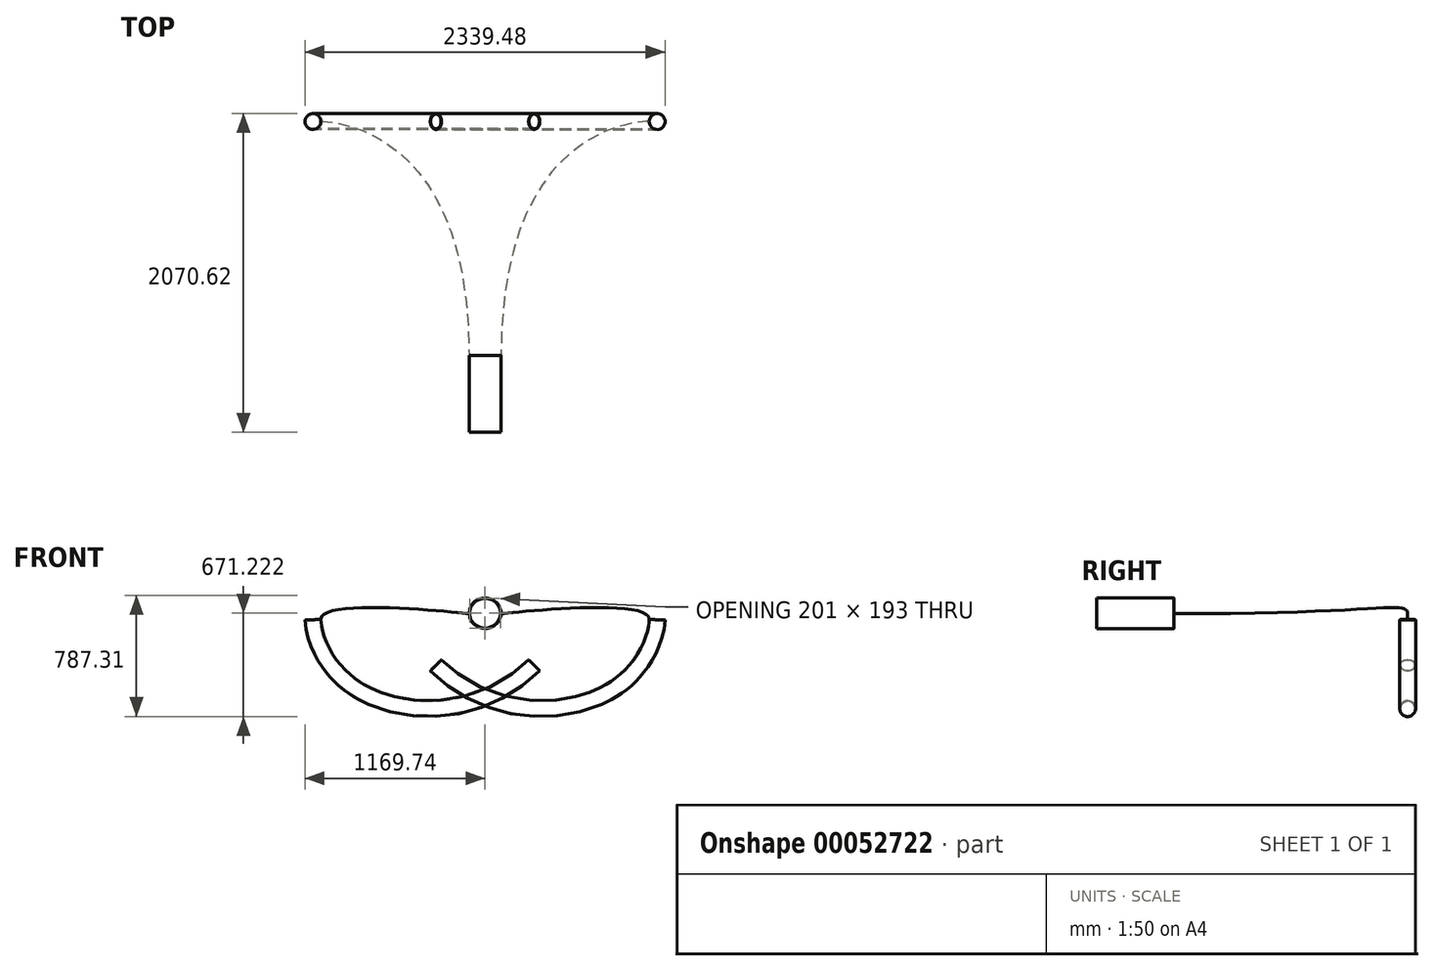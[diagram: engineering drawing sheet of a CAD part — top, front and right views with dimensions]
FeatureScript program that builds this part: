
annotation { "Feature Type Name" : "Feature", "Feature Type Description" : "" }
export const myFeature = defineFeature(function(context is Context, id is Id, definition is map)
    precondition{}
    {
        {
            var Q0;
            Q0=qCreatedBy(makeId("Front.planeOp"),FACE);
            var sketch = newSketch(context, id + "F0", { "sketchPlane" : qUnion([Q0])});
            skLineSegment(sketch, "E0", {"start": v(-822.07, 0) * mm, "end": v(894.41, 0) * mm, "construction": true});
            skLineSegment(sketch, "E1", {"start": v(0, 0) * mm, "end": v(0, 896.06) * mm, "construction": true});
            skLineSegment(sketch, "E2", {"start": v(0, 0) * mm, "end": v(-727.65, 727.65) * mm, "construction": true});
            skLineSegment(sketch, "E3", {"start": v(-854.93, 727.65) * mm, "end": v(-992.18, 590.4) * mm, "construction": true});
            skPoint(sketch, "E4.visualSharp", {"position": v(-791.3, 791.3) * mm});
            skArc(sketch, "E4.filletArc", {"start": v(-727.65, 727.65) * mm, "mid": v(-791.3, 754.01) * mm, "end": v(-854.93, 727.65) * mm, "construction": true});
            skFitSpline(sketch, "E5", {"points": [v(-992.18, 590.4) * mm, v(-770.63, 598.25) * mm, v(-520.2, 137.68) * mm], "startDerivative": vector(522.47, 522.47) * mm, "endDerivative": vector(47.32, -1250.13) * mm});
            skPoint(sketch, "E6", {"position": v(-848.51, 631.85) * mm});
            skFitSpline(sketch, "E7", {"points": [v(1112.9, 903.67) * mm, v(1334.45, 911.52) * mm, v(1584.9, 450.95) * mm], "startDerivative": vector(522.47, 522.47) * mm, "endDerivative": vector(47.32, -1250.13) * mm});
            skPoint(sketch, "E8", {"position": v(-555, 332.37) * mm});
            skSolve(sketch);
        }
        {
            var Q0;
            Q0=sQuery(id+"F0.wireOp",EDGE,"E2");
            var Q1;
            Q1=qCreatedBy(makeId("Top.planeOp"),FACE);
            cPlane(context, id + "F1", {"entities" : qUnion([Q0, Q1]), "cplaneType" : CPlaneType.LINE_ANGLE, "offset" : 150 * mm, "angle" : 0 * degree, "width" : 150 * mm, "height" : 150 * mm});
        }
        {
            var Q0;
            Q0=qCreatedBy(id+"F1.planeOp",FACE);
            cPlane(context, id + "F2", {"entities" : qUnion([Q0]), "cplaneType" : CPlaneType.OFFSET, "offset" : 284.1 * mm, "width" : 150 * mm, "height" : 150 * mm});
        }
        {
            var Q0;
            Q0=qCreatedBy(id+"F2.planeOp",FACE);
            var sketch = newSketch(context, id + "F3", { "sketchPlane" : qUnion([Q0])});
            skCircle(sketch, "E9", {"center": v(-1119.06, 0) * mm, "radius": 51.5 * mm});
            skSolve(sketch);
        }
        {
            var Q0;
            Q0=makeQuery(id+"F3.imprint","IMPRINT",FACE,{"disambiguationData":[TD([[makeQuery(id+"F3.imprint","IMPRINT",EDGE,{"derivedFrom":sQuery(id+"F3.wireOp",EDGE,"E9")}),1.0]])]});
            var Q1;
            Q1=sQuery(id+"F0.wireOp",EDGE,"E5");
            sweep(context, id + "F4", {"profiles" : qUnion([Q0]), "path" : qUnion([Q1])});
        }
        {
            var Q0;
            Q0=qCreatedBy(makeId("Right.planeOp"),FACE);
            cPlane(context, id + "F5", {"entities" : qUnion([Q0]), "cplaneType" : CPlaneType.OFFSET, "offset" : 520.2 * mm, "oppositeDirection" : true, "width" : 150 * mm, "height" : 150 * mm});
        }
        {
            var Q0;
            Q0=makeQuery(id+"F4.opSweep","SWEPT_BODY",BODY,{"disambiguationData":[OSD([sQuery(id+"F0.wireOp",EDGE,"E5"),sQuery(id+"F3.wireOp",EDGE,"E9")])]});
            var Q1;
            Q1=qCreatedBy(id+"F5.planeOp",FACE);
            mirror(context, id + "F6", {"entities" : qUnion([Q0]), "mirrorPlane" : qUnion([Q1])});
        }
        {
            var Q0;
            Q0=qCreatedBy(makeId("Front.planeOp"),FACE);
            cPlane(context, id + "F7", {"entities" : qUnion([Q0]), "cplaneType" : CPlaneType.OFFSET, "offset" : 400 * mm, "width" : 150 * mm, "height" : 150 * mm});
        }
        {
            var Q0;
            Q0=qCreatedBy(id+"F7.planeOp",FACE);
            var sketch = newSketch(context, id + "F8", { "sketchPlane" : qUnion([Q0])});
            skEllipse(sketch, "E10", {"center": v(-520.2, 137.68) * mm, "majorRadius": 104 * mm, "minorRadius": 100 * mm, "majorAxis": v(-1, 0)});
            skSolve(sketch);
        }
        {
            var Q1;
            Q1=makeQuery(id+"F6.opPattern","COPY",FACE,{"derivedFrom":makeQuery(id+"F4.opSweep","CAP_FACE",FACE,{"disambiguationData":[OSD([sQuery(id+"F0.wireOp",VERTEX,"E5.end"),sQuery(id+"F3.wireOp",EDGE,"E9")])],"isStart":false}),"instanceName":"1"});
            var Q2;
            Q2=makeQuery(id+"F8.imprint","IMPRINT",FACE,{"disambiguationData":[TD([[makeQuery(id+"F8.imprint","IMPRINT",EDGE,{"derivedFrom":sQuery(id+"F8.wireOp",EDGE,"E10")}),1.0]])]});
            loft(context, id + "F9", {"startCondition" : LoftEndDerivativeType.NORMAL_TO_PROFILE, "startMagnitude" : 2.5, "endCondition" : LoftEndDerivativeType.NORMAL_TO_PROFILE, "endMagnitude" : 3, "sheetProfilesArray" : [{ "sheetProfileEntities" : qUnion([Q1]) }, { "sheetProfileEntities" : qUnion([Q2]) }]});
        }
        {
            var Q1;
            Q1=makeQuery(id+"F4.opSweep","CAP_FACE",FACE,{"disambiguationData":[OSD([sQuery(id+"F0.wireOp",VERTEX,"E5.end"),sQuery(id+"F3.wireOp",EDGE,"E9")])],"isStart":false});
            var Q2;
            Q2=makeQuery(id+"F8.imprint","IMPRINT",FACE,{"disambiguationData":[TD([[makeQuery(id+"F8.imprint","IMPRINT",EDGE,{"derivedFrom":sQuery(id+"F8.wireOp",EDGE,"E10")}),1.0]])]});
            loft(context, id + "F10", {"startCondition" : LoftEndDerivativeType.NORMAL_TO_PROFILE, "startMagnitude" : 2.5, "endCondition" : LoftEndDerivativeType.NORMAL_TO_PROFILE, "endMagnitude" : 3, "sheetProfilesArray" : [{ "sheetProfileEntities" : qUnion([Q1]) }, { "sheetProfileEntities" : qUnion([Q2]) }]});
        }
        {
            var Q0;
            Q0=makeQuery(id+"F8.imprint","IMPRINT",FACE,{"disambiguationData":[TD([[makeQuery(id+"F8.imprint","IMPRINT",EDGE,{"derivedFrom":sQuery(id+"F8.wireOp",EDGE,"E10")}),1.0]])]});
            extrude(context, id + "F11", {"entities" : qUnion([Q0]), "depth" : 500 * mm});
        }
        {
            var Q0;
            Q0=makeQuery(id+"F4.opSweep","CAP_FACE",FACE,{"disambiguationData":[OSD([sQuery(id+"F0.wireOp",VERTEX,"E5.start"),sQuery(id+"F3.wireOp",EDGE,"E9")])],"isStart":true});
            var Q1;
            Q1=makeQuery(id+"F4.opSweep","CAP_FACE",FACE,{"disambiguationData":[OSD([sQuery(id+"F0.wireOp",VERTEX,"E5.end"),sQuery(id+"F3.wireOp",EDGE,"E9")])],"isStart":false});
            var Q2;
            Q2=makeQuery(id+"F6.opPattern","COPY",FACE,{"derivedFrom":makeQuery(id+"F4.opSweep","CAP_FACE",FACE,{"disambiguationData":[OSD([sQuery(id+"F0.wireOp",VERTEX,"E5.start"),sQuery(id+"F3.wireOp",EDGE,"E9")])],"isStart":true}),"instanceName":"1"});
            var Q3;
            Q3=makeQuery(id+"F6.opPattern","COPY",FACE,{"derivedFrom":makeQuery(id+"F4.opSweep","CAP_FACE",FACE,{"disambiguationData":[OSD([sQuery(id+"F0.wireOp",VERTEX,"E5.end"),sQuery(id+"F3.wireOp",EDGE,"E9")])],"isStart":false}),"instanceName":"1"});
            var Q4;
            Q4=makeQuery(id+"F11.opExtrude","CAP_FACE",FACE,{"disambiguationData":[OSD([sQuery(id+"F8.wireOp",EDGE,"E10")])],"isStart":false});
            var Q5;
            Q5=makeQuery(id+"F11.opExtrude","CAP_FACE",FACE,{"disambiguationData":[OSD([sQuery(id+"F8.wireOp",EDGE,"E10")])],"isStart":true});
            var Q6;
            Q6=makeQuery(id+"F10.opLoft","CAP_FACE",FACE,{"disambiguationData":[OSD([makeQuery(id+"F8.imprint","IMPRINT",FACE,{"disambiguationData":[TD([[makeQuery(id+"F8.imprint","IMPRINT",EDGE,{"derivedFrom":sQuery(id+"F8.wireOp",EDGE,"E10")}),1.0]])]})])],"isStart":true});
            var Q7;
            Q7=makeQuery(id+"F9.opLoft","CAP_FACE",FACE,{"disambiguationData":[OSD([makeQuery(id+"F8.imprint","IMPRINT",FACE,{"disambiguationData":[TD([[makeQuery(id+"F8.imprint","IMPRINT",EDGE,{"derivedFrom":sQuery(id+"F8.wireOp",EDGE,"E10")}),1.0]])]})])],"isStart":true});
            shell(context, id + "F12", {"entities" : qUnion([Q0, Q1, Q2, Q3, Q4, Q5, Q6, Q7]), "thickness" : 3.5 * mm});
        }
    });
